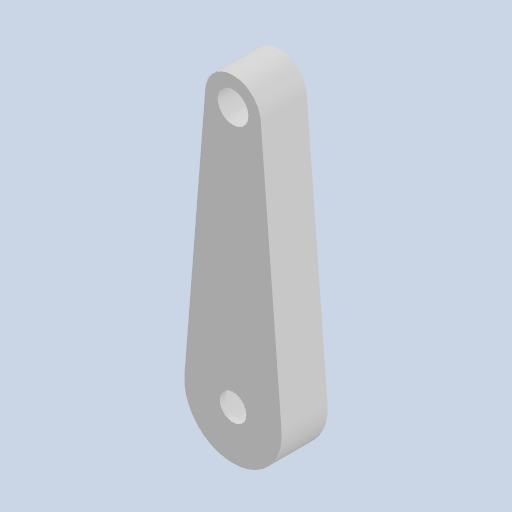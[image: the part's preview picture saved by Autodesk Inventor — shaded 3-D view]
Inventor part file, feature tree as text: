
AUTODESK INVENTOR PART (.ipt)
format: ipt  version: 2022 (Build 260153000, 153)  size: 129,536 bytes
history: native  units: mm
features: other x6, reference x3, extrude x2, sketch x2, projected_geometry x1
ambient origin geometry x8: Origin, YZ Plane, XZ Plane, XY Plane, X Axis, Y Axis, Z Axis, Center Point
bodies: Body1 (feature_tree)
feature tree (14):
  other  "Твердое тело1"
  extrude  "Выдавливание1"  Depth=3.8mm
  extrude  "Выдавливание2"  Depth=7.0mm
  sketch  "Эскиз1"
  reference  "Ссылка1"
  reference  "Ссылка2"
  reference  "Ссылка3"
  sketch  "Эскиз2"
  projected_geometry  "Спроецированная петля1"
  other  "<userpath>\Documents\Git\MZCAT_2024\MZCAT.iam"
  other  "MZCAT.iam"
  other  "OCS-D008 B:1"
  other  "vydacha_chertezh:1"
  other  "plan:1"
